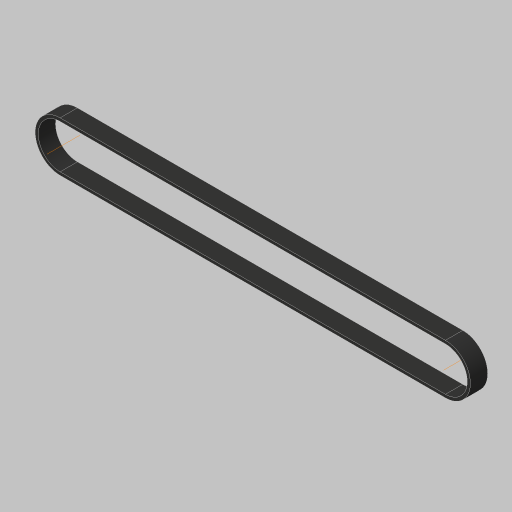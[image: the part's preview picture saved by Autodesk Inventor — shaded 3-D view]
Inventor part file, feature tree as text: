
AUTODESK INVENTOR PART (.ipt)
format: ipt  version: 2023.5 (Build 275446000, 446)  size: 161,280 bytes
history: native  units: in
note: dims shown in document units (in); Inventor stores cm internally (conversion verified against a paired STEP export)
features: sketch x3, extrude x1, other x1, projected_geometry x1
ambient origin geometry x8: Origin, YZ Plane, XZ Plane, XY Plane, X Axis, Y Axis, Z Axis, Center Point
bodies: Body1 (feature_tree)
feature tree (6):
  sketch  "Sketch2"  dims[d0=0.9023in d1=0.9023in]
  extrude  "Extrusion2"  Depth=0.9023in
  sketch  "Sketch5"  dims[d3=1.4174in d5=7.4409in d9=0.0787in d10=0.0598in d11=0.0299in d12=0.0219in d13=0.0219in d14=0.0059in d15=0.0059in d20=0.3346in d21=0.0in d22=0.0787in d23=0.0598in d24=0.0299in d25=0.0219in d26=0.0219in d27=0.0059in d28=0.0059in d29=0.0299in d30=0.0394in d31=0.0787in d32=0.0232in d34=0.0219in d35=0.0in d36=0.0in d37=0.0059in d38=0.0022in d39=0.0022in d40=0.0in d41=0.0in d42=0.0081in d43=0.0081in d44=0.0299in]
  other  "Work Axis1"
  sketch  "Sketch4"  dims[d2=1.4174in]
  projected_geometry  "Projected Loop1"
